# Revit family: PF_ST_BalconyDrain_ACO_2022
name_source: partatom
category: Plumbing Fixtures
units: mm (PartAtom-declared; Revit-internal decimal feet)

## family parameters
Always vertical = No
Cut with Voids When Loaded = Yes
Maintain Annotation Orientation = No
OmniClass Number = 23.70.50.24
OmniClass Title = Rainwater Removal
Part Type = Normal
Room Calculation Point = No
Round Connector Dimension = Use Diameter
Shared = No
Work Plane-Based = Yes

## types (3) — shared parameters
Default Elevation = 1219 mm
Description = Shallow drainage
Fax = +61 2 4747 4040
IfcDescription = Shallow drainage
IfcExportAs = IfcWasteTerminalType
IfcExportType = USERDEFINED
Installation guidelines = www.acobuildline.com.au/product-support/downloads
Maintenance guidelines = www.acobuildline.com.au/product-support/downloads
Manufacturer = ACO Pty Ltd
Model = BalconyDrain
Product_brochure = www.acobuildline.com.au/product-support/downloads
Product_page_URL = www.acobuildline.com.au/products/balconydrain/
Telephone = +61 2 4747 4000
URL = www.acobuildline.com.au
gm_type1 = gratings_BalconyDrain : Affiner_grating
lookup_table_name = BalconyDrain

## per-type parameters (varying)
| type | Assembly Code | connector_position_Z | grate_width | grate_width_tile | type_index | visible_1 | visible_2 | width_01_C_ANZRS | width_C_ANZRS |
| BalconyDrain - 103 x 40 mm |  | 40 mm  [stored 0.131234 ft] | 97 mm  [stored 0.318241 ft] | 87 mm  [stored 0.285433 ft] | 3 | No | Yes | 103 mm  [stored 0.337927 ft] | 103 mm  [stored 0.337927 ft] |
| BalconyDrain - 85 x 25 mm |  | 25 mm  [stored 0.082021 ft] | 79 mm  [stored 0.259186 ft] | 69 mm  [stored 0.226378 ft] | 1 | Yes | No | 85 mm  [stored 0.278871 ft] | 85 mm  [stored 0.278871 ft] |
| BalconyDrain - 103 x 25 mm | D2040300 | 25 mm  [stored 0.082021 ft] | 97 mm  [stored 0.318241 ft] | 87 mm  [stored 0.285433 ft] | 2 | Yes | No | 103 mm  [stored 0.337927 ft] | 103 mm  [stored 0.337927 ft] |

note: [stored X ft] marks values corroborated as IEEE doubles in the binary element streams (Revit-internal decimal feet)

## geometry (parser evidence)
native form markers: Blend x4, Sweep x24
no freeform markers — native parametric forms only
